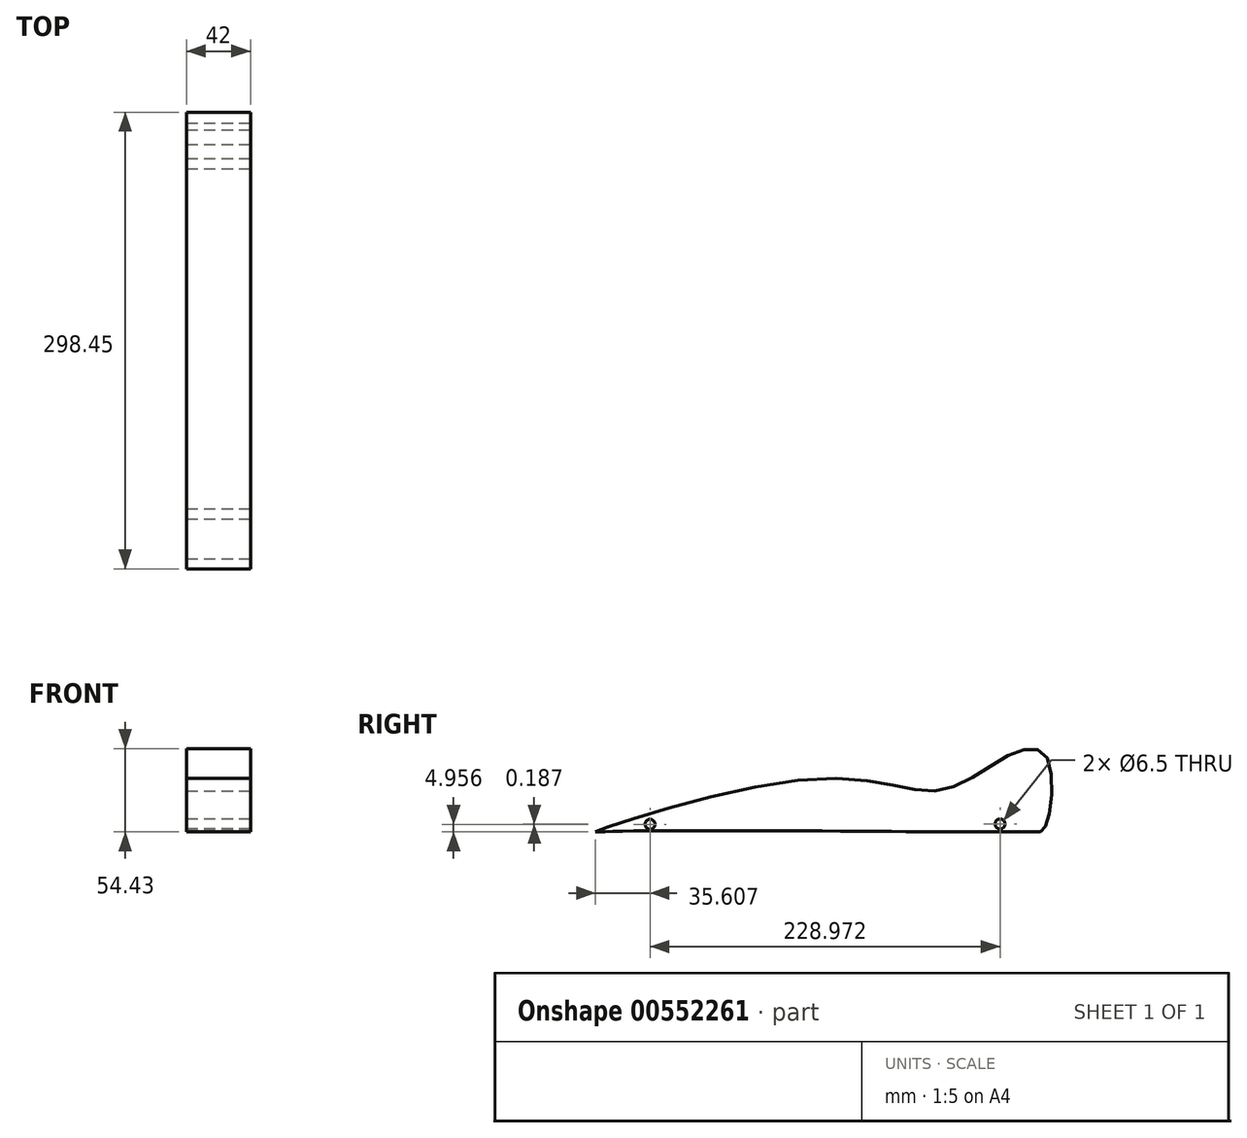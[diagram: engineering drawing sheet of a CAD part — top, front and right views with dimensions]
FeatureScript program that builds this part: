
annotation { "Feature Type Name" : "Feature", "Feature Type Description" : "" }
export const myFeature = defineFeature(function(context is Context, id is Id, definition is map)
    precondition{}
    {
        {
            var Q0;
            Q0=qCreatedBy(makeId("Right.planeOp"),FACE);
            var sketch = newSketch(context, id + "F0", { "sketchPlane" : qUnion([Q0])});
            skLineSegment(sketch, "E0.bottom", {"start": v(150, -35) * mm, "end": v(-150, -35) * mm});
            skLineSegment(sketch, "E0.left", {"start": v(150, -35) * mm, "end": v(150, 35) * mm});
            skLineSegment(sketch, "E0.right", {"start": v(-150, -35) * mm, "end": v(-150, -15) * mm});
            skPoint(sketch, "E0.middle", {"position": v(0, 0) * mm});
            skLineSegment(sketch, "E1", {"start": v(150, 35) * mm, "end": v(-150, -15) * mm});
            skPoint(sketch, "E0.top.end.orphan", {"position": v(-150, 35) * mm});
            skCircle(sketch, "E2", {"center": v(-114.4, -30.04) * mm, "radius": 3.25 * mm});
            skCircle(sketch, "E3", {"center": v(114.58, -29.86) * mm, "radius": 3.25 * mm});
            skFitSpline(sketch, "E4", {"points": [v(-150, -35) * mm, v(0, 0) * mm, v(77.3, -7.44) * mm, v(123.12, 16.41) * mm, v(144.46, 14.84) * mm, v(146.03, -25.64) * mm, v(141, -35) * mm, v(136.61, -35) * mm, v(127.2, -35) * mm, v(118.41, -35) * mm, v(108.05, -35) * mm, v(98.32, -35) * mm, v(82.63, -35) * mm, v(-143.65, -35) * mm, v(-150, -35) * mm]});
            skSolve(sketch);
        }
        {
            var Q0;
            Q0=makeQuery(id+"F0.imprint","IMPRINT",FACE,{"disambiguationData":[TD([[makeQuery(id+"F0.imprint","IMPRINT",EDGE,{"derivedFrom":sQuery(id+"F0.wireOp",EDGE,"E0.bottom")}),-1.0]])]});
            extrude(context, id + "F1", {"entities" : qUnion([Q0]), "endBound" : BoundingType.SYMMETRIC, "depth" : 42 * mm, "offsetDistance" : 25 * mm});
        }
    });
